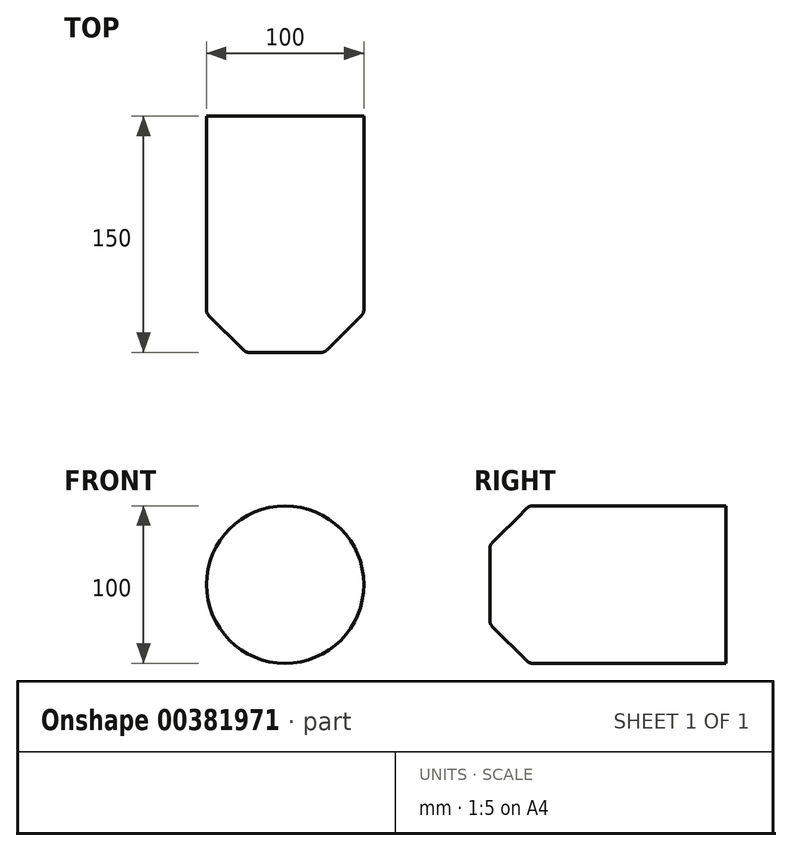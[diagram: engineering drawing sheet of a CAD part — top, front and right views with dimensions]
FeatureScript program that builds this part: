
annotation { "Feature Type Name" : "Feature", "Feature Type Description" : "" }
export const myFeature = defineFeature(function(context is Context, id is Id, definition is map)
    precondition{}
    {
        {
            var Q0;
            Q0=qCreatedBy(makeId("Front.planeOp"),FACE);
            var sketch = newSketch(context, id + "F0", { "sketchPlane" : qUnion([Q0])});
            skCircle(sketch, "E0", {"center": v(0, 0) * mm, "radius": 50 * mm});
            skSolve(sketch);
        }
        {
            var Q0;
            Q0 = qSketchRegion(id + "F0", true);
            extrude(context, id + "F1", {"entities" : qUnion([Q0]), "depth" : 150 * mm});
        }
        {
            var Q0;
            Q0=makeQuery(id+"F1.opExtrude","CAP_FACE",FACE,{"disambiguationData":[OSD([sQuery(id+"F0.wireOp",EDGE,"E0")])],"isStart":false});
            chamfer(context, id + "F2", {"entities" : qUnion([Q0]), "width" : 25 * mm, "tangentPropagation" : true});
        }
        {
            var Q0;
            Q0=makeQuery(id+"F2.opChamfer","BLEND_FACE",FACE,{"disambiguationData":[OSD([sQuery(id+"F0.wireOp",EDGE,"E0")])]});
            fillet(context, id + "F3", {"entities" : qUnion([Q0]), "radius" : 5 * mm, "tangentPropagation" : true, "allowEdgeOverflow" : false});
        }
    });
